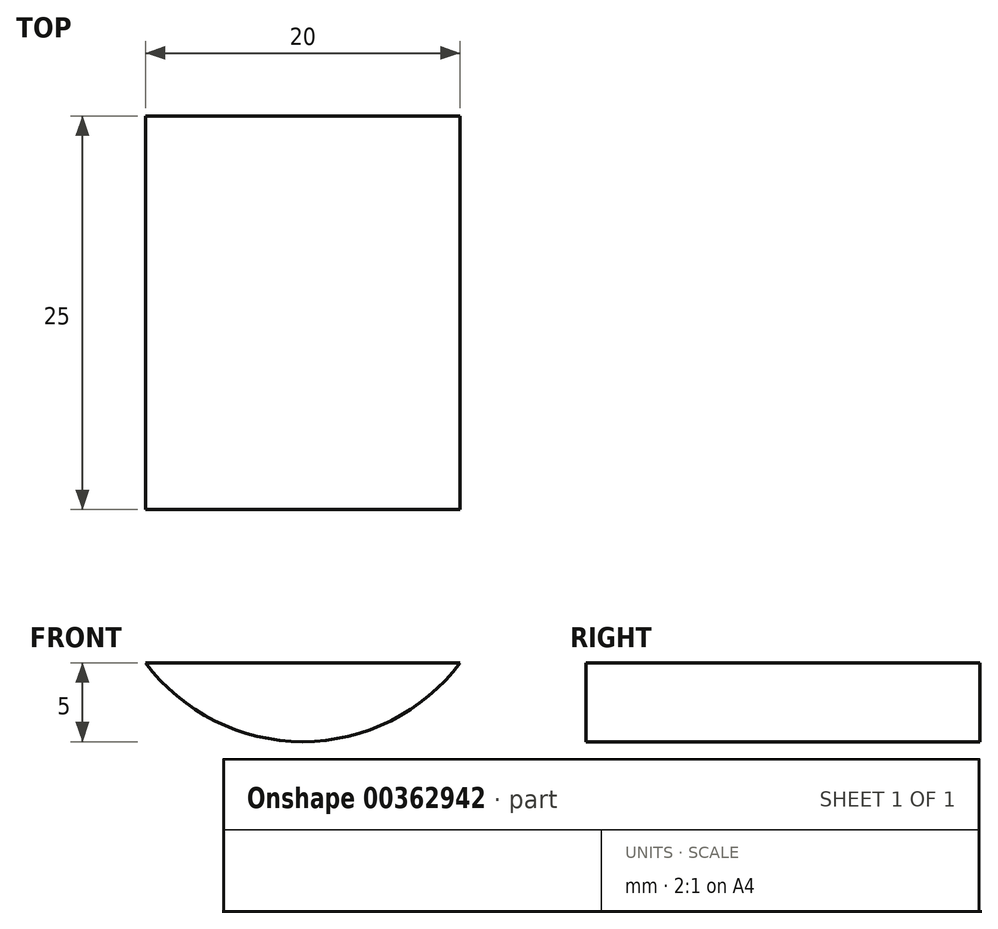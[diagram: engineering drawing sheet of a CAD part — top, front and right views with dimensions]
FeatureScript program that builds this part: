
annotation { "Feature Type Name" : "Feature", "Feature Type Description" : "" }
export const myFeature = defineFeature(function(context is Context, id is Id, definition is map)
    precondition{}
    {
        {
            var Q0;
            Q0=qCreatedBy(makeId("Front.planeOp"),FACE);
            var sketch = newSketch(context, id + "F0", { "sketchPlane" : qUnion([Q0])});
            skArc(sketch, "E0", {"start": v(-10, -7.5) * mm, "mid": v(0, -12.5) * mm, "end": v(10, -7.5) * mm});
            skLineSegment(sketch, "E1", {"start": v(-10, -7.5) * mm, "end": v(10, -7.5) * mm});
            skSolve(sketch);
        }
        {
            var Q0;
            Q0=makeQuery(id+"F0.imprint","IMPRINT",FACE,{"disambiguationData":[TD([[makeQuery(id+"F0.imprint","IMPRINT",EDGE,{"derivedFrom":sQuery(id+"F0.wireOp",EDGE,"E0")}),1.0]])]});
            extrude(context, id + "F1", {"entities" : qUnion([Q0]), "depth" : 25 * mm});
        }
    });
